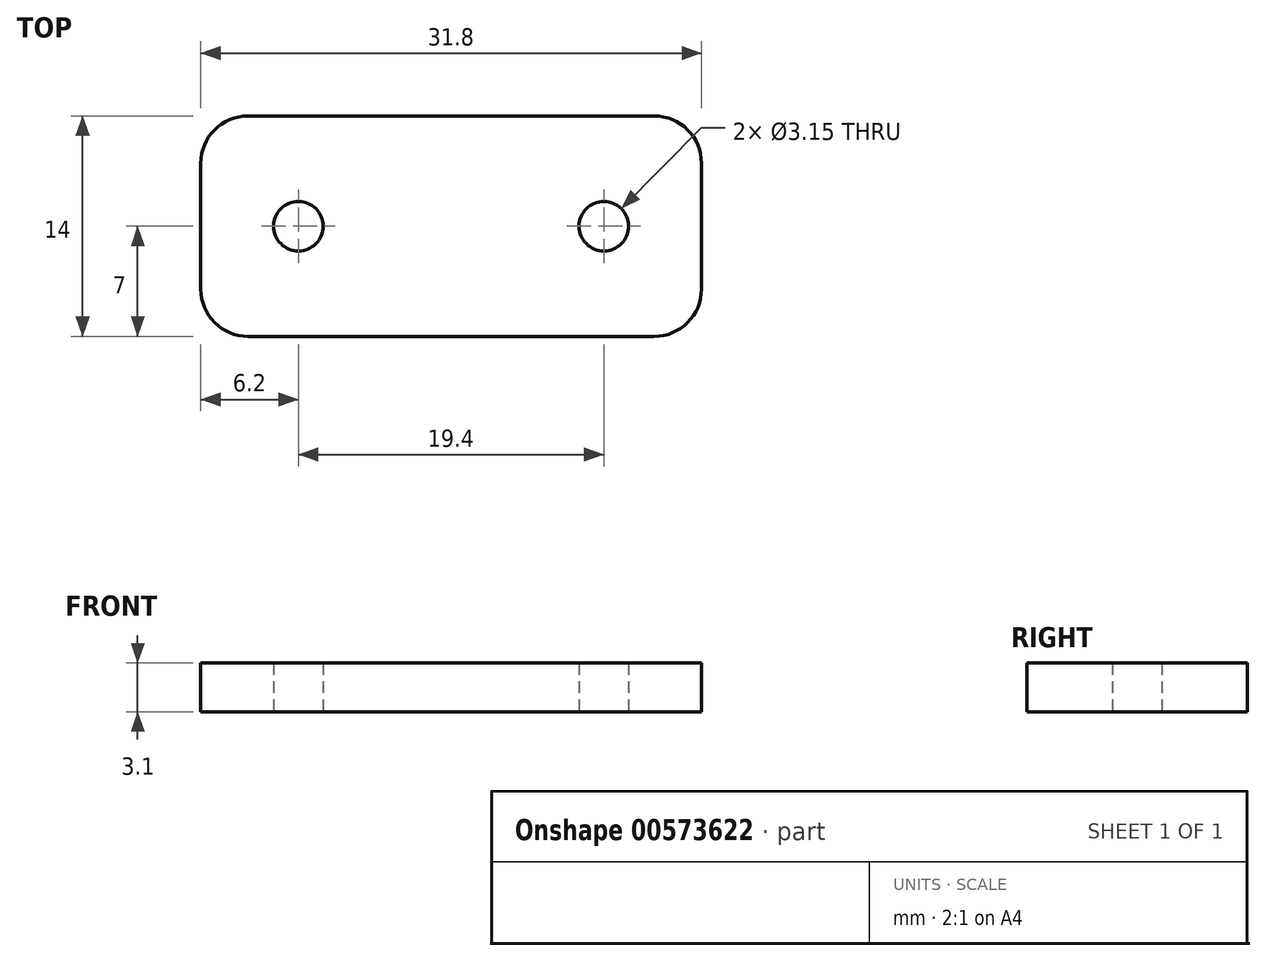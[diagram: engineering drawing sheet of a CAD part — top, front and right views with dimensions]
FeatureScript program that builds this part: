
annotation { "Feature Type Name" : "Feature", "Feature Type Description" : "" }
export const myFeature = defineFeature(function(context is Context, id is Id, definition is map)
    precondition{}
    {
        {
            var Q0;
            Q0=qCreatedBy(makeId("Top.planeOp"),FACE);
            var sketch = newSketch(context, id + "F0", { "sketchPlane" : qUnion([Q0])});
            skLineSegment(sketch, "E0.bottom", {"start": v(15.9, -7) * mm, "end": v(-15.9, -7) * mm});
            skLineSegment(sketch, "E0.top", {"start": v(15.9, 7) * mm, "end": v(-15.9, 7) * mm});
            skLineSegment(sketch, "E0.left", {"start": v(15.9, -7) * mm, "end": v(15.9, 7) * mm});
            skLineSegment(sketch, "E0.right", {"start": v(-15.9, -7) * mm, "end": v(-15.9, 7) * mm});
            skPoint(sketch, "E0.middle", {"position": v(0, 0) * mm});
            skCircle(sketch, "E1", {"center": v(-9.7, 0) * mm, "radius": 1.57 * mm});
            skLineSegment(sketch, "E2", {"start": v(0, 7) * mm, "end": v(0, -7) * mm, "construction": true});
            skCircle(sketch, "E3.MirrorC", {"center": v(9.7, 0) * mm, "radius": 1.57 * mm});
            skCircle(sketch, "E4", {"center": v(-9.7, 0) * mm, "radius": 2.2 * mm, "construction": true});
            skCircle(sketch, "E5", {"center": v(9.7, 0) * mm, "radius": 2.2 * mm, "construction": true});
            skSolve(sketch);
        }
        {
            var Q0;
            Q0 = qSketchRegion(id + "F0", true);
            extrude(context, id + "F1", {"entities" : qUnion([Q0]), "depth" : 3.1 * mm, "offsetDistance" : 25 * mm});
        }
        {
            var Q0;
            Q0=makeQuery(id+"F1.opExtrude","SWEPT_EDGE",EDGE,{"disambiguationData":[OSD([sQuery(id+"F0.wireOp",EDGE,"E0.bottom"),sQuery(id+"F0.wireOp",EDGE,"E0.right")])]});
            var Q1;
            Q1=makeQuery(id+"F1.opExtrude","SWEPT_EDGE",EDGE,{"disambiguationData":[OSD([sQuery(id+"F0.wireOp",EDGE,"E0.bottom"),sQuery(id+"F0.wireOp",EDGE,"E0.left")])]});
            var Q2;
            Q2=makeQuery(id+"F1.opExtrude","SWEPT_EDGE",EDGE,{"disambiguationData":[OSD([sQuery(id+"F0.wireOp",EDGE,"E0.top"),sQuery(id+"F0.wireOp",EDGE,"E0.right")])]});
            var Q3;
            Q3=makeQuery(id+"F1.opExtrude","SWEPT_EDGE",EDGE,{"disambiguationData":[OSD([sQuery(id+"F0.wireOp",EDGE,"E0.top"),sQuery(id+"F0.wireOp",EDGE,"E0.left")])]});
            fillet(context, id + "F2", {"entities" : qUnion([Q0, Q1, Q2, Q3]), "radius" : 3 * mm, "tangentPropagation" : true, "allowEdgeOverflow" : false});
        }
    });
